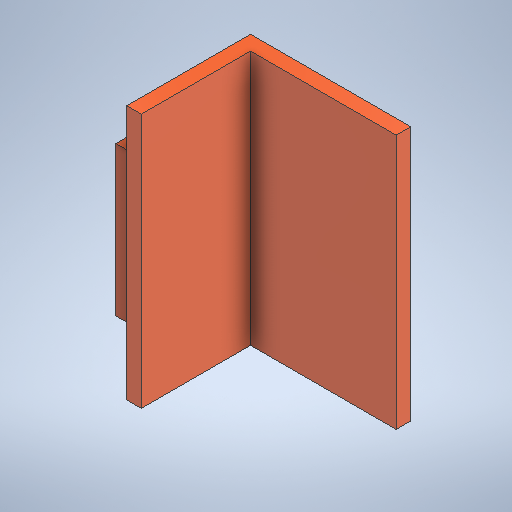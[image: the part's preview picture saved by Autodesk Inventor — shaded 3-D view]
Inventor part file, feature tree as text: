
AUTODESK INVENTOR PART (.ipt)
format: ipt  version: 2025.1 (Build 291241020, 241B)  size: 246,272 bytes
history: native  units: in
note: dims shown in document units (in); Inventor stores cm internally (conversion verified against a paired STEP export)
features: extrude x3, sketch x3
ambient origin geometry x8: Origin, YZ Plane, XZ Plane, XY Plane, X Axis, Y Axis, Z Axis, Center Point
bodies: Solid1 (feature_tree)
feature tree (6):
  extrude  "Extrusion1"  Depth=1.378in
  extrude  "Extrusion2"  Depth=0.0787in
  extrude  "Extrusion3"  Depth=0.8071in
  sketch  "Sketch1"  dims[d0=0.8661in d1=1.378in]
  sketch  "Sketch2"  dims[d2=0.0787in d3=0.0in d4=0.0787in]
  sketch  "Sketch3"  dims[d5=0.5906in d6=0.0in d7=0.8071in d8=0.0787in d9=0.2756in d10=0.0787in d11=0.5709in d12=0.1378in d13=0.0in]
